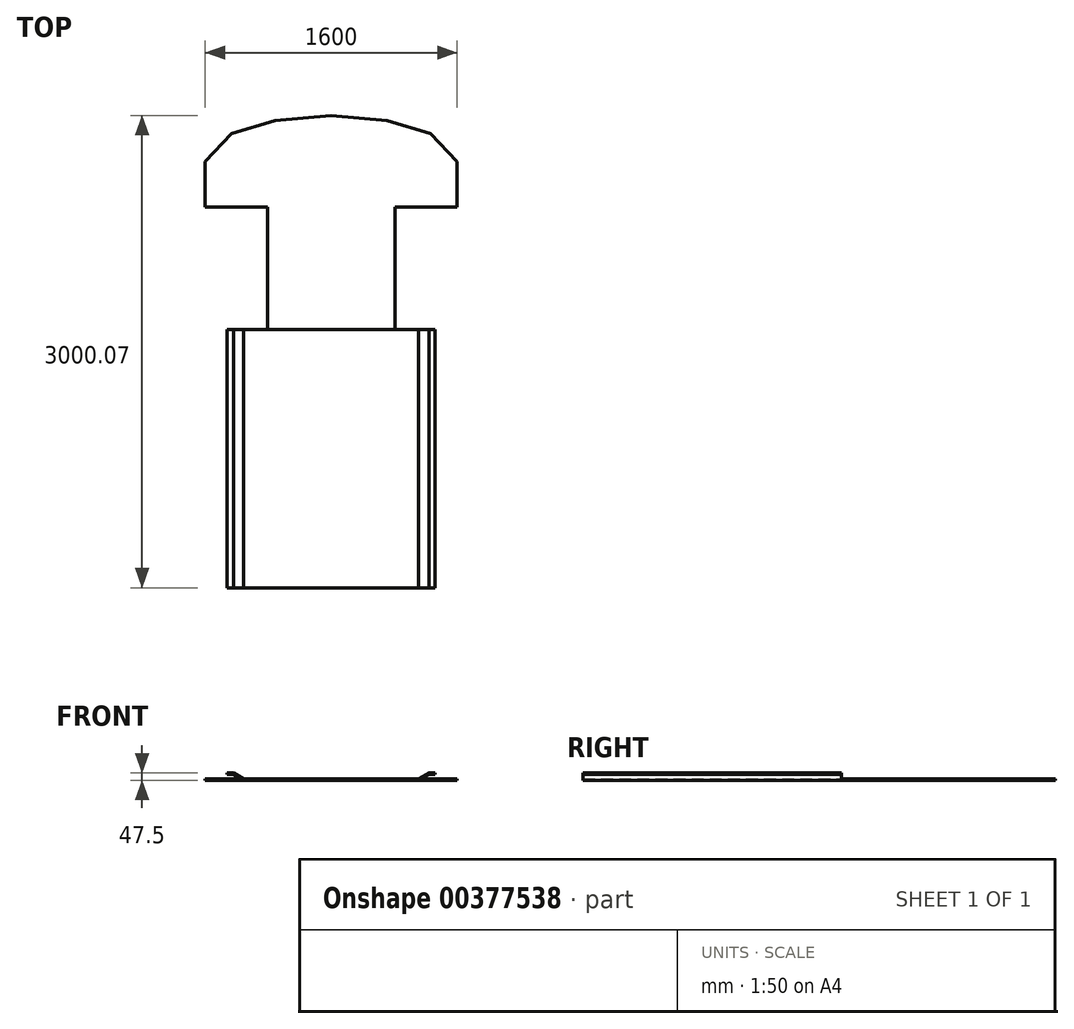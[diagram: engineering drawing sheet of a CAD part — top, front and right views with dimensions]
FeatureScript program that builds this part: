
annotation { "Feature Type Name" : "Feature", "Feature Type Description" : "" }
export const myFeature = defineFeature(function(context is Context, id is Id, definition is map)
    precondition{}
    {
        {
            var Q0;
            Q0=qCreatedBy(makeId("Front.planeOp"),FACE);
            var sketch = newSketch(context, id + "F0", { "sketchPlane" : qUnion([Q0])});
            skLineSegment(sketch, "E0", {"start": v(0, 0) * mm, "end": v(555.05, 0) * mm});
            skLineSegment(sketch, "E1", {"start": v(555.05, 0) * mm, "end": v(620, 37.5) * mm});
            skLineSegment(sketch, "E2", {"start": v(620, 37.5) * mm, "end": v(660, 37.5) * mm});
            skLineSegment(sketch, "E3", {"start": v(0, 0) * mm, "end": v(0, -10) * mm});
            skLineSegment(sketch, "E4", {"start": v(0, -10) * mm, "end": v(555.05, -10) * mm});
            skLineSegment(sketch, "E5", {"start": v(555.05, -10) * mm, "end": v(620, 27.5) * mm});
            skLineSegment(sketch, "E6", {"start": v(620, 27.5) * mm, "end": v(660, 27.5) * mm});
            skLineSegment(sketch, "E7", {"start": v(660, 27.5) * mm, "end": v(660, 37.5) * mm});
            skLineSegment(sketch, "E8.MirrorCS", {"start": v(-660, 27.5) * mm, "end": v(-660, 37.5) * mm});
            skLineSegment(sketch, "E9.MirrorCS", {"start": v(-620, 27.5) * mm, "end": v(-660, 27.5) * mm});
            skLineSegment(sketch, "E10.MirrorCS", {"start": v(0, -10) * mm, "end": v(-555.05, -10) * mm});
            skLineSegment(sketch, "E11.MirrorCS", {"start": v(-555.05, -10) * mm, "end": v(-620, 27.5) * mm});
            skLineSegment(sketch, "E12.MirrorCS", {"start": v(-555.05, 0) * mm, "end": v(-620, 37.5) * mm});
            skLineSegment(sketch, "E13.MirrorCS", {"start": v(0, 0) * mm, "end": v(-555.05, 0) * mm});
            skLineSegment(sketch, "E14.MirrorCS", {"start": v(-620, 37.5) * mm, "end": v(-660, 37.5) * mm});
            skSolve(sketch);
        }
        {
            var Q0;
            Q0=qCreatedBy(makeId("Top.planeOp"),FACE);
            var sketch = newSketch(context, id + "F1", { "sketchPlane" : qUnion([Q0])});
            skLineSegment(sketch, "E15.bottom", {"start": v(0, 820.07) * mm, "end": v(405, 820.07) * mm});
            skLineSegment(sketch, "E15.top", {"start": v(0, 1600.07) * mm, "end": v(405, 1600.07) * mm});
            skLineSegment(sketch, "E15.right", {"start": v(405, 820.07) * mm, "end": v(405, 1600.07) * mm});
            skLineSegment(sketch, "E16.bottom", {"start": v(0, 1600.07) * mm, "end": v(800, 1600.07) * mm});
            skLineSegment(sketch, "E16.right", {"start": v(800, 1600.07) * mm, "end": v(800, 1888.04) * mm});
            skLineSegment(sketch, "E17", {"start": v(0, 2180.07) * mm, "end": v(355.87, 2147.39) * mm});
            skLineSegment(sketch, "E18", {"start": v(355.87, 2147.39) * mm, "end": v(632.12, 2066.73) * mm});
            skLineSegment(sketch, "E19", {"start": v(632.12, 2066.73) * mm, "end": v(800, 1888.04) * mm});
            skLineSegment(sketch, "E20", {"start": v(800, 1888.04) * mm, "end": v(800, 1600.07) * mm});
            skLineSegment(sketch, "E21.MirrorCS", {"start": v(0, 1600.07) * mm, "end": v(-405, 1600.07) * mm});
            skLineSegment(sketch, "E22.MirrorCS", {"start": v(-405, 820.07) * mm, "end": v(-405, 1600.07) * mm});
            skLineSegment(sketch, "E23.MirrorCS", {"start": v(0, 820.07) * mm, "end": v(-405, 820.07) * mm});
            skLineSegment(sketch, "E24", {"start": v(0, -819.93) * mm, "end": v(0, 820.07) * mm});
            skLineSegment(sketch, "E25", {"start": v(0, 2180.07) * mm, "end": v(0, 1600.07) * mm});
            skLineSegment(sketch, "E26.MirrorCS", {"start": v(-800, 1600.07) * mm, "end": v(-800, 1888.04) * mm});
            skLineSegment(sketch, "E27.MirrorCS", {"start": v(-800, 1888.04) * mm, "end": v(-800, 1600.07) * mm});
            skLineSegment(sketch, "E28.MirrorCS", {"start": v(-632.12, 2066.73) * mm, "end": v(-800, 1888.04) * mm});
            skLineSegment(sketch, "E29.MirrorCS", {"start": v(-355.87, 2147.39) * mm, "end": v(-632.12, 2066.73) * mm});
            skLineSegment(sketch, "E30.MirrorCS", {"start": v(0, 2180.07) * mm, "end": v(-355.87, 2147.39) * mm});
            skLineSegment(sketch, "E31.MirrorCS", {"start": v(0, 1600.07) * mm, "end": v(-800, 1600.07) * mm});
            skSolve(sketch);
        }
        {
            var Q0;
            Q0 = qSketchRegion(id + "F0", true);
            extrude(context, id + "F2", {"entities" : qUnion([Q0]), "endBound" : BoundingType.SYMMETRIC, "depth" : 1640 * mm});
        }
        {
            var Q0;
            Q0 = qSketchRegion(id + "F1", true);
            extrude(context, id + "F3", {"entities" : qUnion([Q0]), "oppositeDirection" : true, "depth" : 10 * mm});
        }
    });
